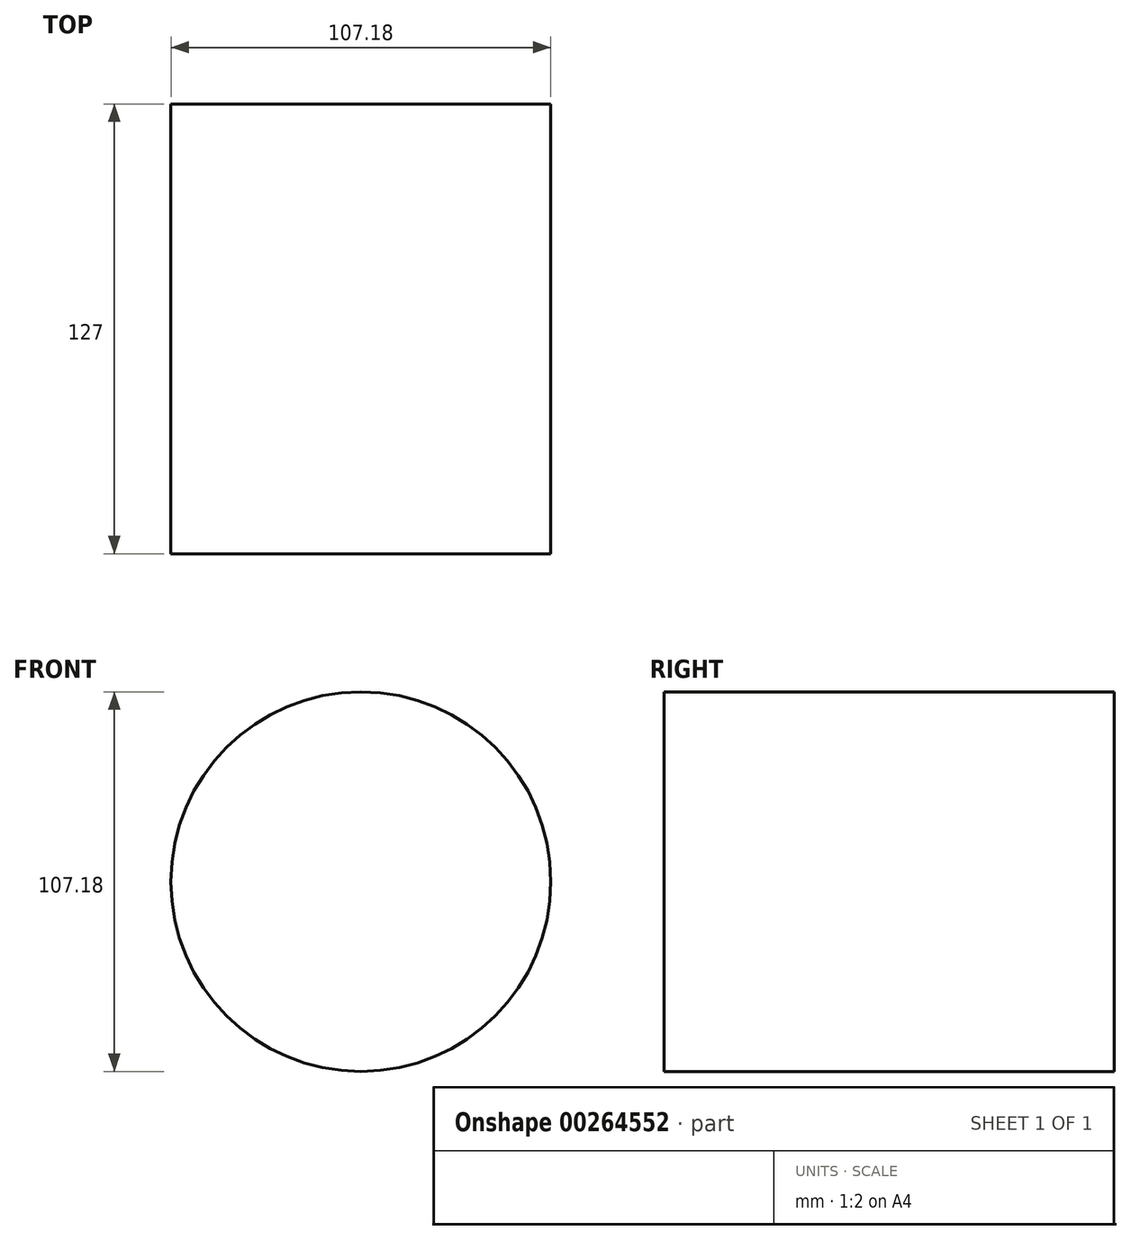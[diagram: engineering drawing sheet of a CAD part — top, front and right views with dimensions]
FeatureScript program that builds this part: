
annotation { "Feature Type Name" : "Feature", "Feature Type Description" : "" }
export const myFeature = defineFeature(function(context is Context, id is Id, definition is map)
    precondition{}
    {
        {
            var Q0;
            Q0=qCreatedBy(makeId("Front.planeOp"),FACE);
            var sketch = newSketch(context, id + "F0", { "sketchPlane" : qUnion([Q0])});
            skCircle(sketch, "E0", {"center": v(0, 0) * mm, "radius": 53.6 * mm});
            skSolve(sketch);
        }
        {
            var Q0;
            Q0=makeQuery(id+"F0.imprint","IMPRINT",FACE,{"disambiguationData":[TD([[makeQuery(id+"F0.imprint","IMPRINT",EDGE,{"derivedFrom":sQuery(id+"F0.wireOp",EDGE,"E0")}),1.0]])]});
            extrude(context, id + "F1", {"entities" : qUnion([Q0]), "depth" : 127 * mm});
        }
    });
